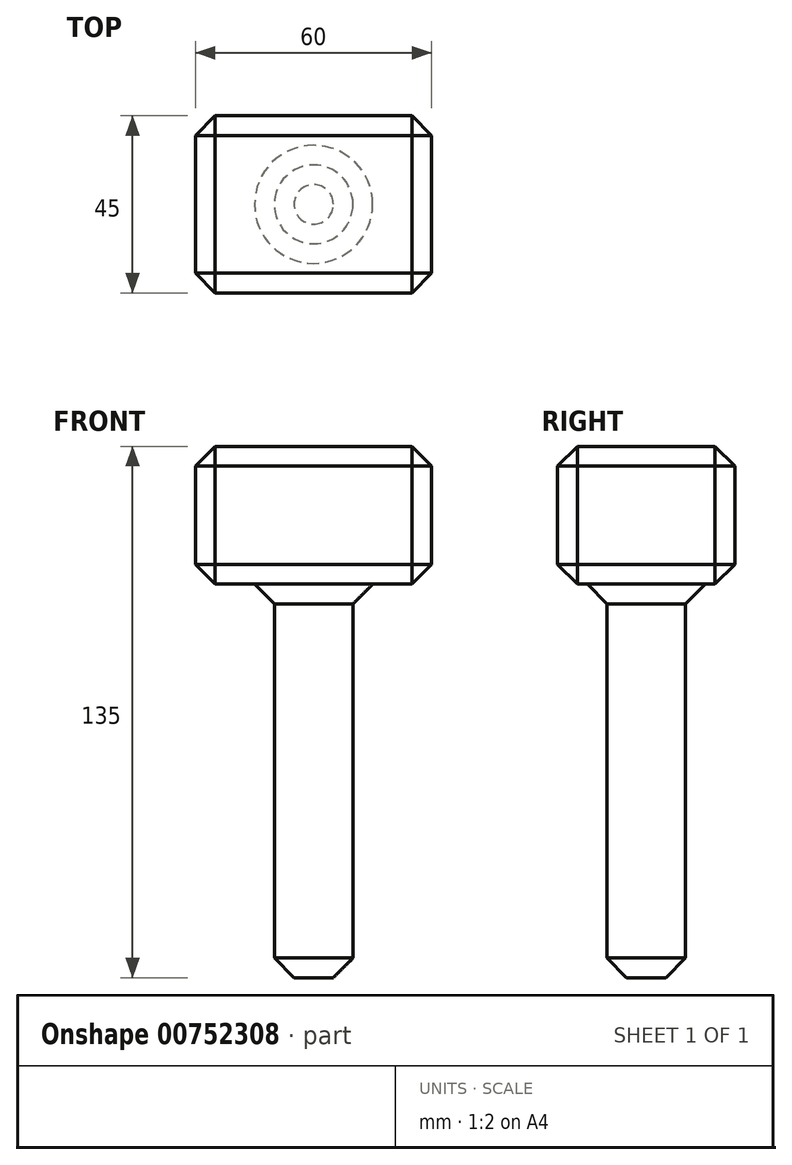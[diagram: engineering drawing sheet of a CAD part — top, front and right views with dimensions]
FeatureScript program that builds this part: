
annotation { "Feature Type Name" : "Feature", "Feature Type Description" : "" }
export const myFeature = defineFeature(function(context is Context, id is Id, definition is map)
    precondition{}
    {
        {
            var Q0;
            Q0=qCreatedBy(makeId("Top.planeOp"),FACE);
            var sketch = newSketch(context, id + "F0", { "sketchPlane" : qUnion([Q0])});
            skLineSegment(sketch, "E0.bottom", {"start": v(30, -22.5) * mm, "end": v(-30, -22.5) * mm});
            skLineSegment(sketch, "E0.top", {"start": v(30, 22.5) * mm, "end": v(-30, 22.5) * mm});
            skLineSegment(sketch, "E0.left", {"start": v(30, -22.5) * mm, "end": v(30, 22.5) * mm});
            skLineSegment(sketch, "E0.right", {"start": v(-30, -22.5) * mm, "end": v(-30, 22.5) * mm});
            skPoint(sketch, "E0.middle", {"position": v(0, 0) * mm});
            skCircle(sketch, "E1", {"center": v(0, 0) * mm, "radius": 10 * mm});
            skSolve(sketch);
        }
        {
            var Q0;
            Q0=makeQuery(id+"F0.imprint","IMPRINT",FACE,{"disambiguationData":[TD([[makeQuery(id+"F0.imprint","IMPRINT",EDGE,{"derivedFrom":sQuery(id+"F0.wireOp",EDGE,"E0.bottom")}),-1.0]])]});
            var Q1;
            Q1=makeQuery(id+"F0.imprint","IMPRINT",FACE,{"disambiguationData":[TD([[makeQuery(id+"F0.imprint","IMPRINT",EDGE,{"derivedFrom":sQuery(id+"F0.wireOp",EDGE,"E1")}),1.0]])]});
            extrude(context, id + "F1", {"entities" : qUnion([Q0, Q1]), "depth" : 35 * mm, "offsetDistance" : 25 * mm});
        }
        {
            var Q0;
            Q0=makeQuery(id+"F0.imprint","IMPRINT",FACE,{"disambiguationData":[TD([[makeQuery(id+"F0.imprint","IMPRINT",EDGE,{"derivedFrom":sQuery(id+"F0.wireOp",EDGE,"E1")}),1.0]])]});
            extrude(context, id + "F2", {"entities" : qUnion([Q0]), "operationType" : NewBodyOperationType.ADD, "oppositeDirection" : true, "depth" : 100 * mm, "offsetDistance" : 25 * mm});
        }
        {
            var Q0;
            Q0=makeQuery(id+"F1.opExtrude","SWEPT_EDGE",EDGE,{"disambiguationData":[OSD([sQuery(id+"F0.wireOp",EDGE,"E0.bottom"),sQuery(id+"F0.wireOp",EDGE,"E0.right")])]});
            var Q1;
            Q1=makeQuery(id+"F1.opExtrude","SWEPT_EDGE",EDGE,{"disambiguationData":[OSD([sQuery(id+"F0.wireOp",EDGE,"E0.bottom"),sQuery(id+"F0.wireOp",EDGE,"E0.left")])]});
            var Q2;
            Q2=makeQuery(id+"F1.opExtrude","SWEPT_EDGE",EDGE,{"disambiguationData":[OSD([sQuery(id+"F0.wireOp",EDGE,"E0.top"),sQuery(id+"F0.wireOp",EDGE,"E0.left")])]});
            var Q3;
            Q3=makeQuery(id+"F1.opExtrude","SWEPT_EDGE",EDGE,{"disambiguationData":[OSD([sQuery(id+"F0.wireOp",EDGE,"E0.top"),sQuery(id+"F0.wireOp",EDGE,"E0.right")])]});
            var Q4;
            Q4=makeQuery(id+"F1.opExtrude","CAP_EDGE",EDGE,{"disambiguationData":[OSD([sQuery(id+"F0.wireOp",EDGE,"E0.top")])],"isStart":false});
            var Q5;
            Q5=makeQuery(id+"F1.opExtrude","CAP_EDGE",EDGE,{"disambiguationData":[OSD([sQuery(id+"F0.wireOp",EDGE,"E0.top")])],"isStart":true});
            var Q6;
            Q6=makeQuery(id+"F1.opExtrude","CAP_EDGE",EDGE,{"disambiguationData":[OSD([sQuery(id+"F0.wireOp",EDGE,"E0.bottom")])],"isStart":false});
            var Q7;
            Q7=makeQuery(id+"F1.opExtrude","CAP_EDGE",EDGE,{"disambiguationData":[OSD([sQuery(id+"F0.wireOp",EDGE,"E0.bottom")])],"isStart":true});
            var Q8;
            Q8=makeQuery(id+"F1.opExtrude","CAP_EDGE",EDGE,{"disambiguationData":[OSD([sQuery(id+"F0.wireOp",EDGE,"E0.right")])],"isStart":true});
            var Q9;
            Q9=makeQuery(id+"F1.opExtrude","CAP_EDGE",EDGE,{"disambiguationData":[OSD([sQuery(id+"F0.wireOp",EDGE,"E0.right")])],"isStart":false});
            var Q10;
            Q10=makeQuery(id+"F1.opExtrude","CAP_EDGE",EDGE,{"disambiguationData":[OSD([sQuery(id+"F0.wireOp",EDGE,"E0.left")])],"isStart":false});
            var Q11;
            Q11=makeQuery(id+"F1.opExtrude","CAP_EDGE",EDGE,{"disambiguationData":[OSD([sQuery(id+"F0.wireOp",EDGE,"E0.left")])],"isStart":true});
            chamfer(context, id + "F3", {"entities" : qUnion([Q0, Q1, Q2, Q3, Q4, Q5, Q6, Q7, Q8, Q9, Q10, Q11]), "width" : 5 * mm, "tangentPropagation" : true});
        }
        {
            var Q0;
            Q0=makeQuery(id+"F2.opExtrude","SWEPT_FACE",FACE,{"disambiguationData":[OSD([sQuery(id+"F0.wireOp",EDGE,"E1")])]});
            chamfer(context, id + "F4", {"entities" : qUnion([Q0]), "width" : 5 * mm, "tangentPropagation" : true});
        }
    });
